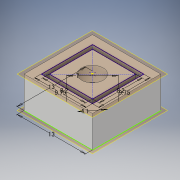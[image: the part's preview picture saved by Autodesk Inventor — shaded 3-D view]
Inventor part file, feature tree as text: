
AUTODESK INVENTOR PART (.ipt)
format: ipt  version: 2019 (Build 230136000, 136)  size: 134,656 bytes
history: native  units: in
note: dims shown in document units (in); Inventor stores cm internally (conversion verified against a paired STEP export)
features: extrude x4, sketch x2, other x1
ambient origin geometry x8: Origin, YZ Plane, XZ Plane, XY Plane, X Axis, Y Axis, Z Axis, Center Point
bodies: Body1 (feature_tree)
feature tree (7):
  other  "作業平面2"
  sketch  "スケッチ3"
  sketch  "スケッチ1"
  extrude  "押し出し8"  Depth=0.2362in
  extrude  "押し出し9"  Depth=0.3228in
  extrude  "押し出し10"  Depth=0.3228in
  extrude  "押し出し11"  Depth=0.3839in
